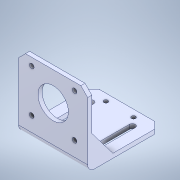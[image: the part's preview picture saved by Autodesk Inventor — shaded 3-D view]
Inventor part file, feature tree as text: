
AUTODESK INVENTOR PART (.ipt)
format: ipt  version: 2022 (Build 260153000, 153)  size: 154,624 bytes
history: mixed  units: in
note: dims shown in document units (in); Inventor stores cm internally (conversion verified against a paired STEP export)
features: extrude x1, sketch x1, fillet x1, imported_body x1
ambient origin geometry x8: Origin, YZ Plane, XZ Plane, XY Plane, X Axis, Y Axis, Z Axis, Center Point
bodies: Solid1 (imported_parasolid)
feature tree (4):
  extrude  "Extrusion2"  TaperAngle=0.0deg  [1 undecoded]
  sketch  "Sketch3"  dims[d11=0.1181in d12=0.0in d13=0.0in d6=0.0197in d7=0.0344in d8=0.0197in d9=0.0344in]
  fillet  "Fillet1"  Radius=0.0197in
  imported_body  NMx_Import_Brep_tag  [imported B-rep: ~34 faces, bbox_mm=[50.0, 52.145, 53.3]]
note: 1 required parameter value undecoded (feature->parameter linkage not recoverable at this tier; creation-order binding heuristic only, values carry confidence <= 0.55)
